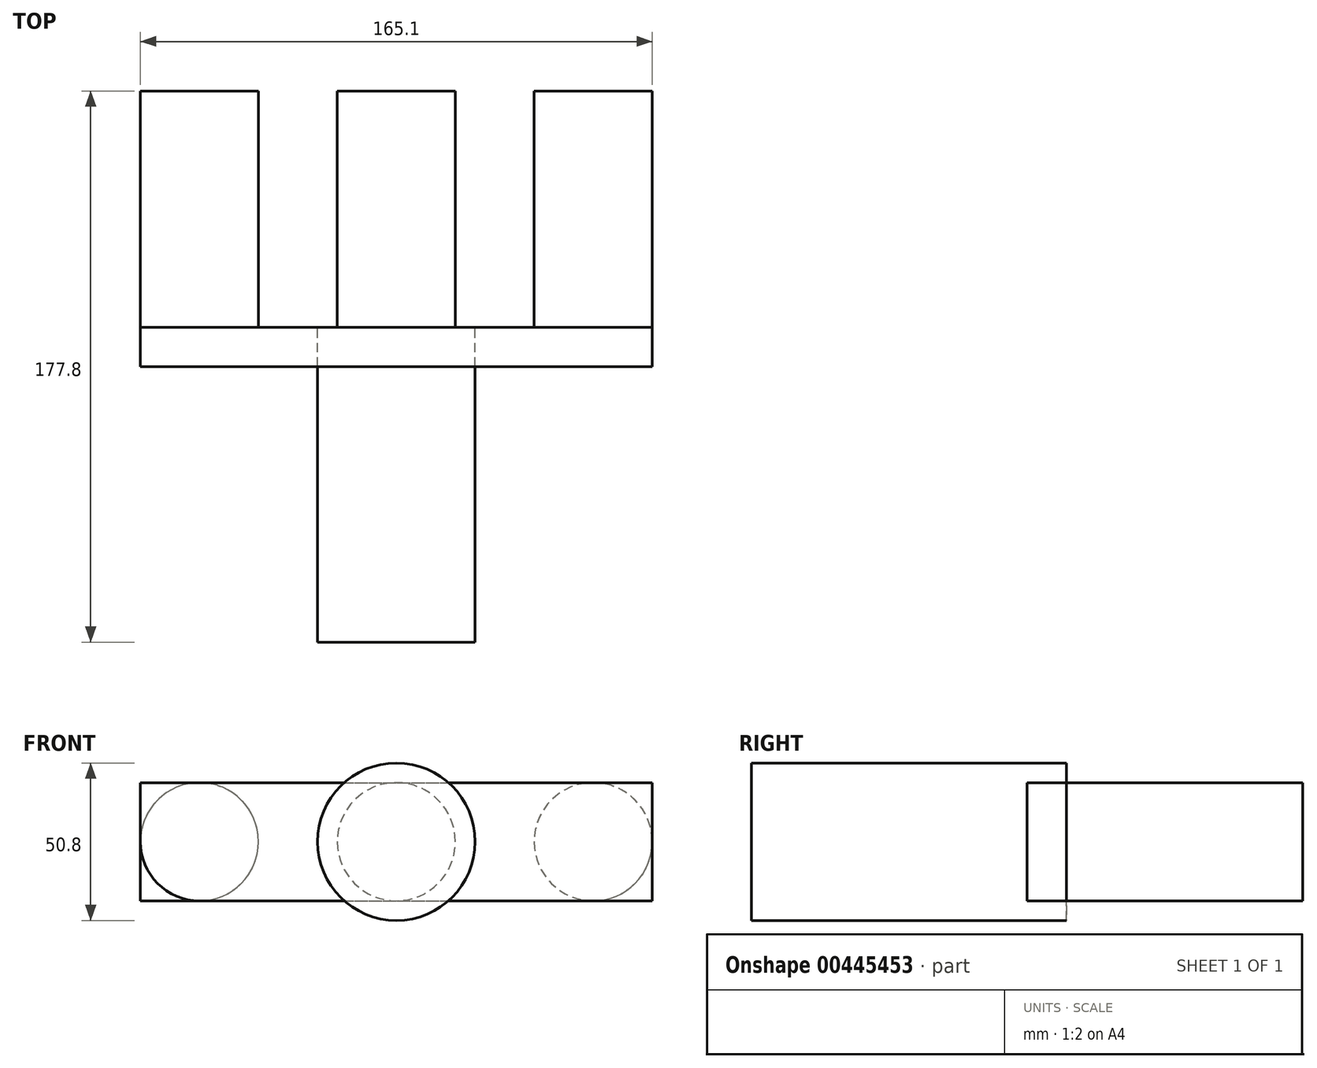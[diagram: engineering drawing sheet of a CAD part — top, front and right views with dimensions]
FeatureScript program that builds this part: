
annotation { "Feature Type Name" : "Feature", "Feature Type Description" : "" }
export const myFeature = defineFeature(function(context is Context, id is Id, definition is map)
    precondition{}
    {
        {
            var Q0;
            Q0=qCreatedBy(makeId("Front.planeOp"),FACE);
            var sketch = newSketch(context, id + "F0", { "sketchPlane" : qUnion([Q0])});
            skLineSegment(sketch, "E0.bottom", {"start": v(-82.55, 19.05) * mm, "end": v(82.55, 19.05) * mm});
            skLineSegment(sketch, "E0.top", {"start": v(-82.55, -19.05) * mm, "end": v(82.55, -19.05) * mm});
            skLineSegment(sketch, "E0.left", {"start": v(-82.55, 19.05) * mm, "end": v(-82.55, -19.05) * mm});
            skLineSegment(sketch, "E0.right", {"start": v(82.55, 19.05) * mm, "end": v(82.55, -19.05) * mm});
            skPoint(sketch, "E0.middle", {"position": v(0, 0) * mm});
            skSolve(sketch);
        }
        {
            var Q0;
            Q0 = qSketchRegion(id + "F0", true);
            extrude(context, id + "F1", {"entities" : qUnion([Q0]), "depth" : 12.7 * mm});
        }
        {
            var Q0;
            Q0=qCreatedBy(makeId("Front.planeOp"),FACE);
            var sketch = newSketch(context, id + "F2", { "sketchPlane" : qUnion([Q0])});
            skCircle(sketch, "E1", {"center": v(0, 0) * mm, "radius": 25.4 * mm});
            skSolve(sketch);
        }
        {
            var Q0;
            Q0=makeQuery(id+"F2.imprint","IMPRINT",FACE,{"disambiguationData":[TD([[makeQuery(id+"F2.imprint","IMPRINT",EDGE,{"derivedFrom":sQuery(id+"F2.wireOp",EDGE,"E1")}),1.0]])]});
            extrude(context, id + "F3", {"entities" : qUnion([Q0]), "depth" : 101.6 * mm});
        }
        {
            var Q0;
            Q0=qCreatedBy(makeId("Front.planeOp"),FACE);
            var sketch = newSketch(context, id + "F4", { "sketchPlane" : qUnion([Q0])});
            skLineSegment(sketch, "E2", {"start": v(0, 0) * mm, "end": v(-63.5, 0) * mm});
            skLineSegment(sketch, "E3", {"start": v(0, 0) * mm, "end": v(63.5, 0) * mm});
            skCircle(sketch, "E4", {"center": v(-63.5, 0) * mm, "radius": 19.05 * mm});
            skCircle(sketch, "E5", {"center": v(0, 0) * mm, "radius": 19.05 * mm});
            skCircle(sketch, "E6", {"center": v(63.5, 0) * mm, "radius": 19.05 * mm});
            skSolve(sketch);
        }
        {
            var Q0;
            Q0 = qSketchRegion(id + "F4", true);
            extrude(context, id + "F5", {"entities" : qUnion([Q0]), "oppositeDirection" : true, "depth" : 76.2 * mm});
        }
    });
